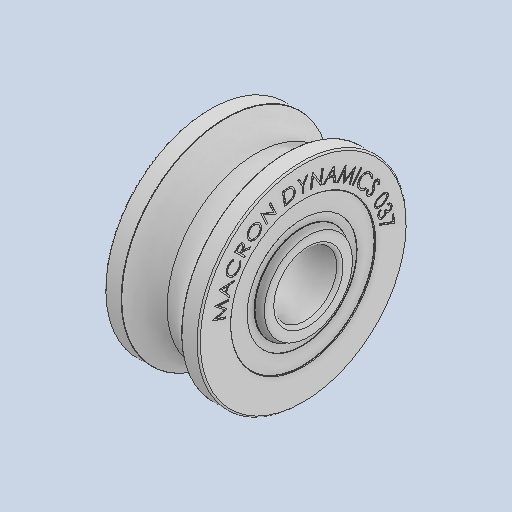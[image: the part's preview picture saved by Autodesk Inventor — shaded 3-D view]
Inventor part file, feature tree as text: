
AUTODESK INVENTOR PART (.ipt)
format: ipt  version: 2022 (Build 260153000, 153)  size: 777,728 bytes
history: native  units: in
note: dims shown in document units (in); Inventor stores cm internally (conversion verified against a paired STEP export)
features: revolve x1, other x1
ambient origin geometry x8: Origin, YZ Plane, XZ Plane, XY Plane, X Axis, Y Axis, Z Axis, Center Point
bodies: Solid1 (feature_tree), Solid2 (feature_tree)
feature tree (2):
  revolve  "Revolve3"  [1 undecoded]
  other  "Cut-Extrude1"
note: 1 required parameter value undecoded (feature->parameter linkage not recoverable at this tier; creation-order binding heuristic only, values carry confidence <= 0.55)
